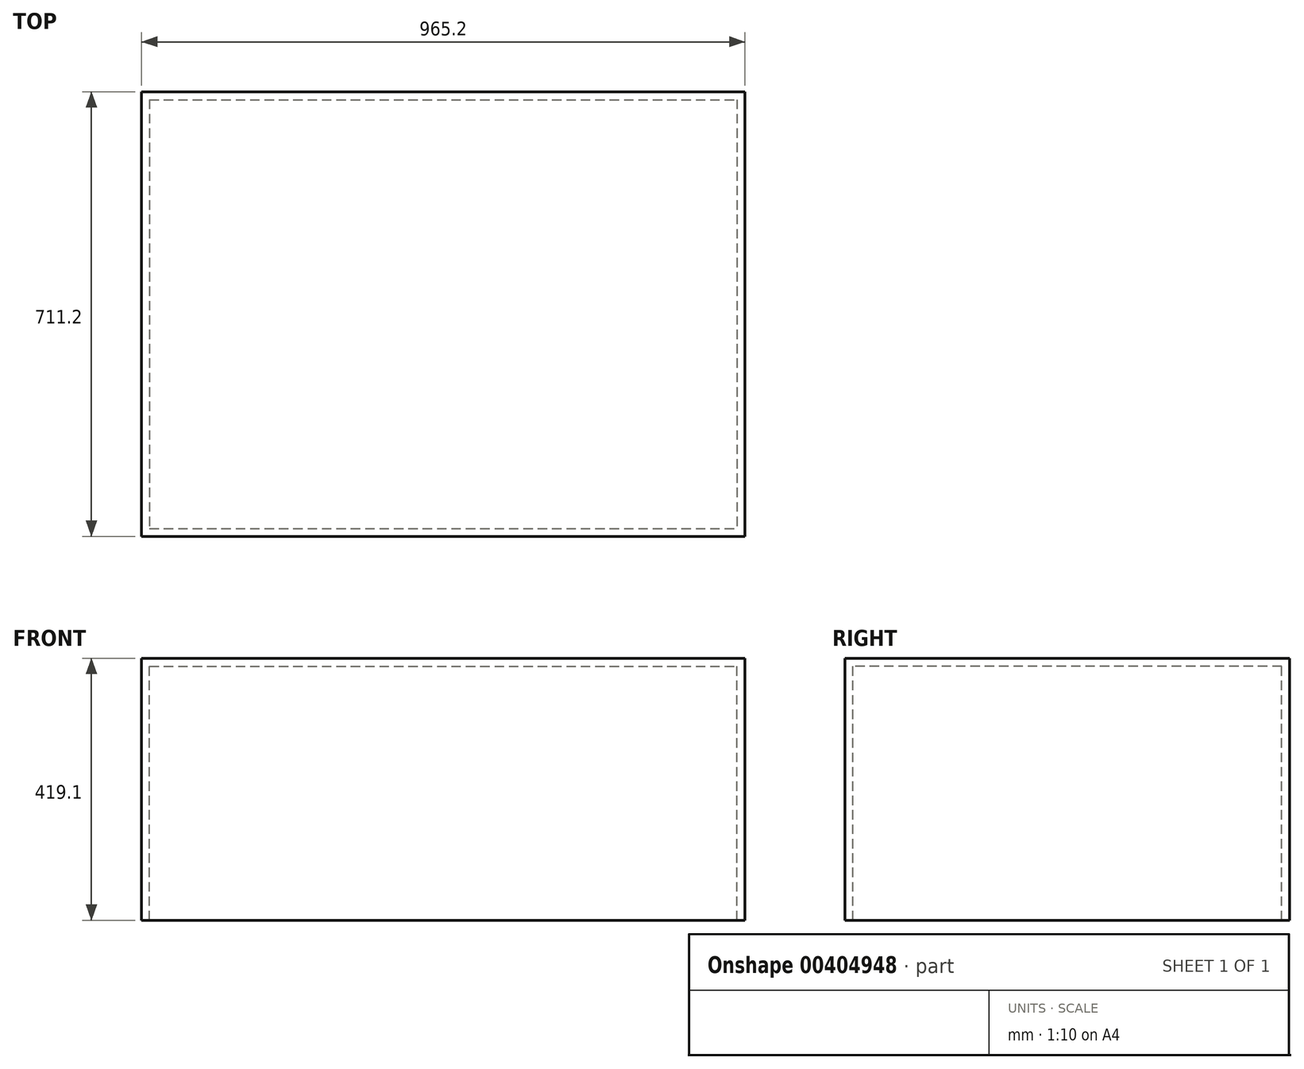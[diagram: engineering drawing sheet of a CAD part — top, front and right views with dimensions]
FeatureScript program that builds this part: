
annotation { "Feature Type Name" : "Feature", "Feature Type Description" : "" }
export const myFeature = defineFeature(function(context is Context, id is Id, definition is map)
    precondition{}
    {
        {
            var Q0;
            Q0=qCreatedBy(makeId("Top.planeOp"),FACE);
            var sketch = newSketch(context, id + "F0", { "sketchPlane" : qUnion([Q0])});
            skLineSegment(sketch, "E0.bottom", {"start": v(0, 0) * mm, "end": v(965.2, 0) * mm});
            skLineSegment(sketch, "E0.top", {"start": v(0, -711.2) * mm, "end": v(965.2, -711.2) * mm});
            skLineSegment(sketch, "E0.left", {"start": v(0, 0) * mm, "end": v(0, -711.2) * mm});
            skLineSegment(sketch, "E0.right", {"start": v(965.2, 0) * mm, "end": v(965.2, -711.2) * mm});
            skSolve(sketch);
        }
        {
            var Q0;
            Q0=makeQuery(id+"F0.imprint","IMPRINT",FACE,{"disambiguationData":[TD([[makeQuery(id+"F0.imprint","IMPRINT",EDGE,{"derivedFrom":sQuery(id+"F0.wireOp",EDGE,"E0.bottom")}),-1.0]])]});
            extrude(context, id + "F1", {"entities" : qUnion([Q0]), "oppositeDirection" : true, "depth" : 12.7 * mm});
        }
        {
            var Q0;
            Q0=makeQuery(id+"F1.opExtrude","CAP_FACE",FACE,{"disambiguationData":[OSD([sQuery(id+"F0.wireOp",EDGE,"E0.bottom"),sQuery(id+"F0.wireOp",EDGE,"E0.top"),sQuery(id+"F0.wireOp",EDGE,"E0.left"),sQuery(id+"F0.wireOp",EDGE,"E0.right")])],"isStart":false});
            var sketch = newSketch(context, id + "F2", { "sketchPlane" : qUnion([Q0])});
            skLineSegment(sketch, "E1.0", {"start": v(0, 711.2) * mm, "end": v(965.2, 711.2) * mm});
            skLineSegment(sketch, "E1.1", {"start": v(965.2, 0) * mm, "end": v(965.2, 711.2) * mm});
            skLineSegment(sketch, "E1.2", {"start": v(0, 0) * mm, "end": v(965.2, 0) * mm});
            skLineSegment(sketch, "E1.3", {"start": v(0, 0) * mm, "end": v(0, 711.2) * mm});
            skLineSegment(sketch, "E2.0", {"start": v(12.7, 12.7) * mm, "end": v(12.7, 698.5) * mm});
            skLineSegment(sketch, "E2.1", {"start": v(12.7, 12.7) * mm, "end": v(952.5, 12.7) * mm});
            skLineSegment(sketch, "E2.2", {"start": v(952.5, 12.7) * mm, "end": v(952.5, 698.5) * mm});
            skLineSegment(sketch, "E2.3", {"start": v(12.7, 698.5) * mm, "end": v(952.5, 698.5) * mm});
            skSolve(sketch);
        }
        {
            var Q0;
            Q0=makeQuery(id+"F2.imprint","IMPRINT",FACE,{"disambiguationData":[TD([[makeQuery(id+"F2.imprint","IMPRINT",EDGE,{"derivedFrom":sQuery(id+"F2.wireOp",EDGE,"E1.0")}),-1.0]])]});
            extrude(context, id + "F3", {"entities" : qUnion([Q0]), "operationType" : NewBodyOperationType.ADD, "depth" : 406.4 * mm});
        }
    });
